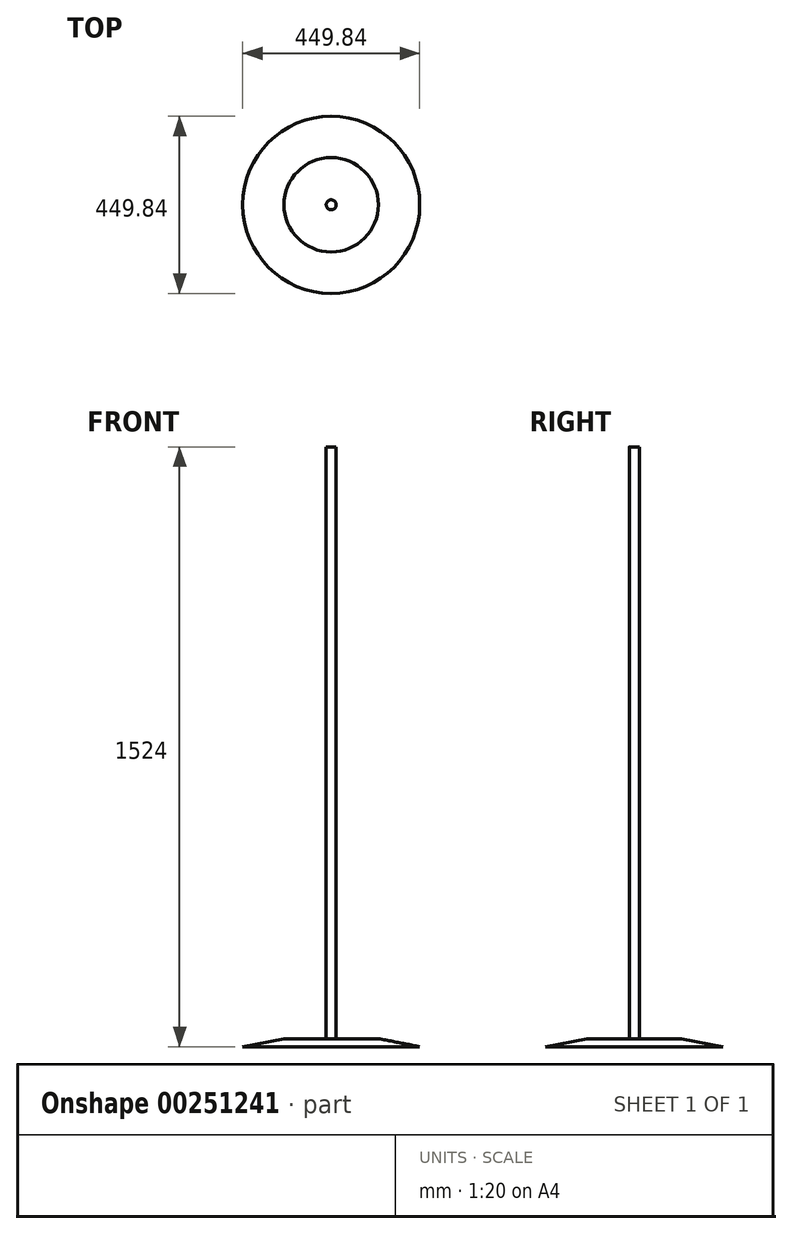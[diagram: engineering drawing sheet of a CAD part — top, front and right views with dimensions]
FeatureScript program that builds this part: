
annotation { "Feature Type Name" : "Feature", "Feature Type Description" : "" }
export const myFeature = defineFeature(function(context is Context, id is Id, definition is map)
    precondition{}
    {
        {
            var Q0;
            Q0=qCreatedBy(makeId("Front.planeOp"),FACE);
            var sketch = newSketch(context, id + "F0", { "sketchPlane" : qUnion([Q0])});
            skLineSegment(sketch, "E0", {"start": v(0, 0) * mm, "end": v(-224.92, 0) * mm});
            skLineSegment(sketch, "E1", {"start": v(-224.92, 0) * mm, "end": v(-119.97, 20.32) * mm});
            skLineSegment(sketch, "E2", {"start": v(-119.97, 20.32) * mm, "end": v(-12.7, 20.32) * mm});
            skLineSegment(sketch, "E3", {"start": v(-12.7, 20.32) * mm, "end": v(-12.7, 1524) * mm});
            skLineSegment(sketch, "E4", {"start": v(-12.7, 1524) * mm, "end": v(0, 1524) * mm});
            skLineSegment(sketch, "E5", {"start": v(0, 1524) * mm, "end": v(0, 0) * mm});
            skSolve(sketch);
        }
        {
            var Q0;
            Q0=makeQuery(id+"F0.imprint","IMPRINT",FACE,{"disambiguationData":[TD([[makeQuery(id+"F0.imprint","IMPRINT",EDGE,{"derivedFrom":sQuery(id+"F0.wireOp",EDGE,"E0")}),-1.0]])]});
            var Q1;
            Q1=sQuery(id+"F0.wireOp",EDGE,"E5");
            revolve(context, id + "F1", {"entities" : qUnion([Q0]), "axis" : qUnion([Q1]), "revolveType" : RevolveType.FULL});
        }
    });
